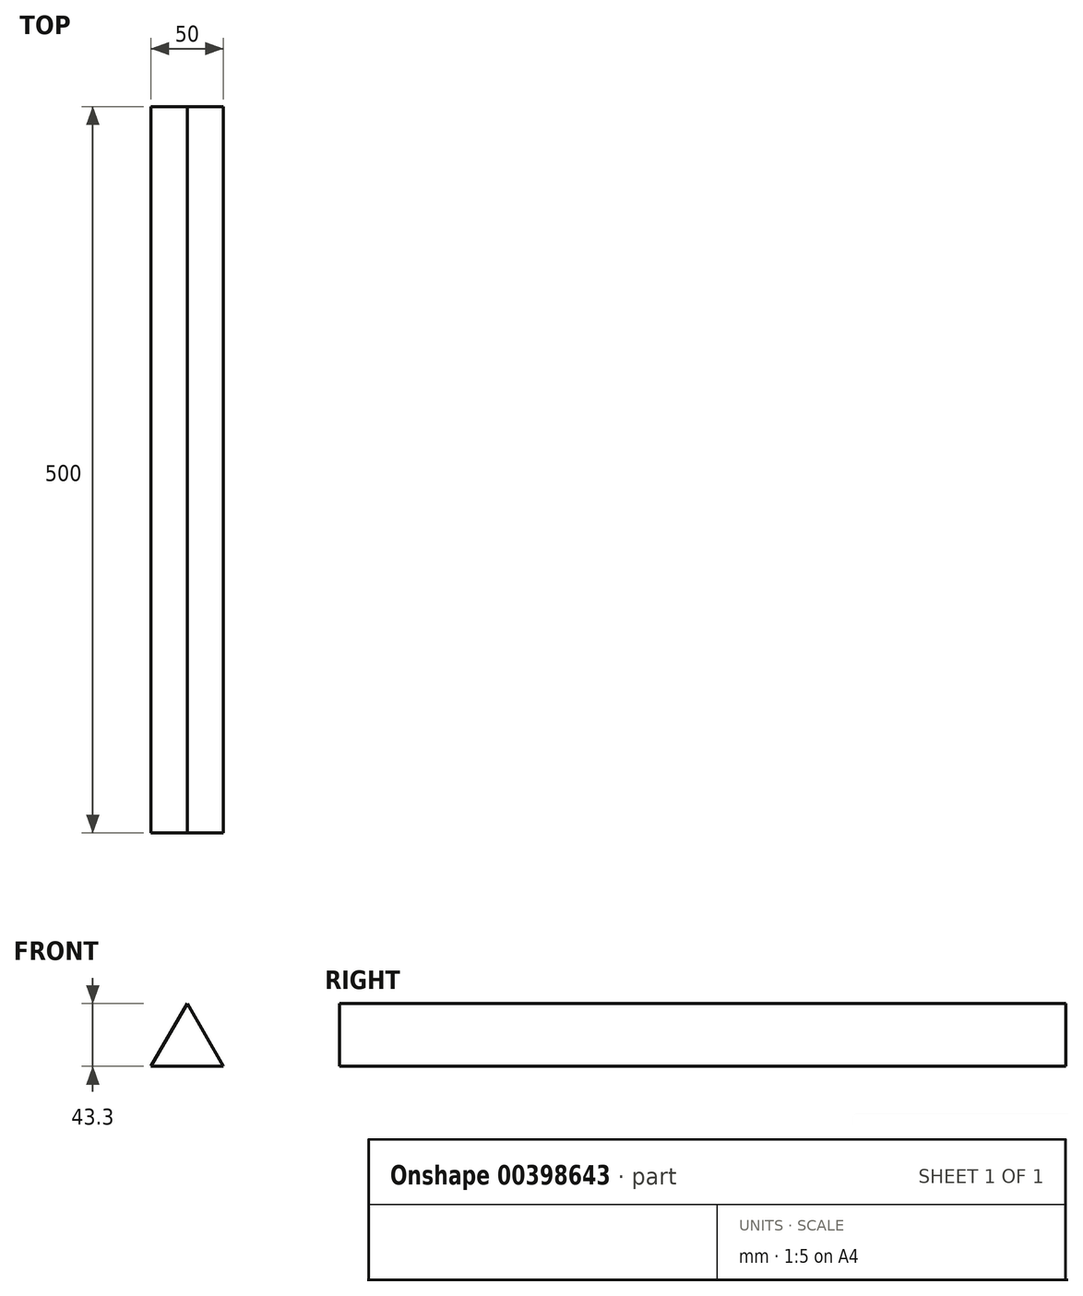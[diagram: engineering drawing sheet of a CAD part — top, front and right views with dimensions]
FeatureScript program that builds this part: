
annotation { "Feature Type Name" : "Feature", "Feature Type Description" : "" }
export const myFeature = defineFeature(function(context is Context, id is Id, definition is map)
    precondition{}
    {
        {
            var Q0;
            Q0=qCreatedBy(makeId("Front.planeOp"),FACE);
            var sketch = newSketch(context, id + "F0", { "sketchPlane" : qUnion([Q0])});
            skLineSegment(sketch, "E0", {"start": v(-25, 0) * mm, "end": v(25, 0) * mm});
            skLineSegment(sketch, "E1", {"start": v(25, 0) * mm, "end": v(0, 43.3) * mm});
            skLineSegment(sketch, "E2", {"start": v(0, 43.3) * mm, "end": v(-25, 0) * mm});
            skSolve(sketch);
        }
        {
            var Q0;
            Q0=makeQuery(id+"F0.imprint","IMPRINT",FACE,{"disambiguationData":[TD([[makeQuery(id+"F0.imprint","IMPRINT",EDGE,{"derivedFrom":sQuery(id+"F0.wireOp",EDGE,"E0")}),1.0]])]});
            extrude(context, id + "F1", {"entities" : qUnion([Q0]), "depth" : 500 * mm});
        }
    });
